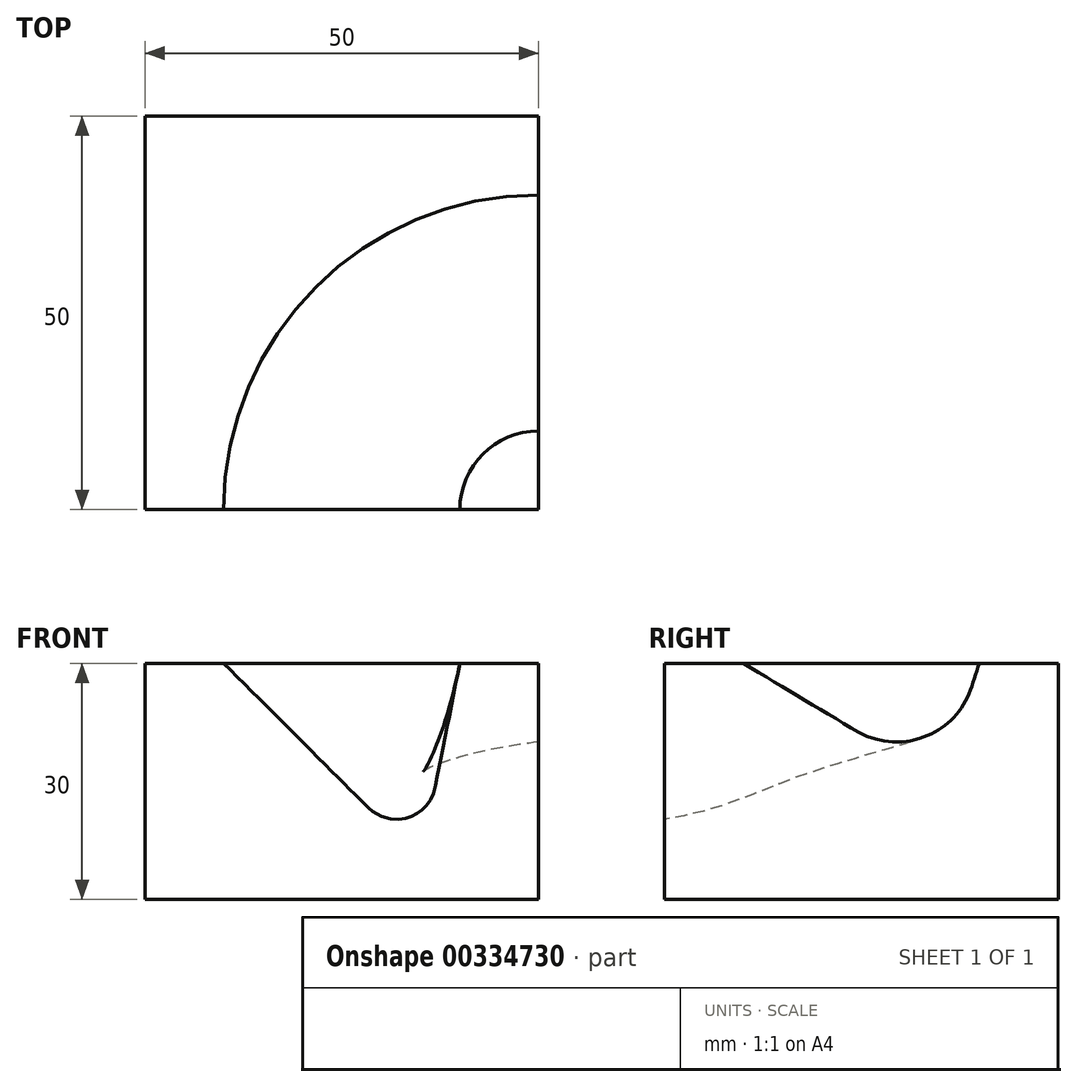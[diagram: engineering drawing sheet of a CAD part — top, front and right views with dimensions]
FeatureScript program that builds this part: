
annotation { "Feature Type Name" : "Feature", "Feature Type Description" : "" }
export const myFeature = defineFeature(function(context is Context, id is Id, definition is map)
    precondition{}
    {
        {
            var Q0;
            Q0=qCreatedBy(makeId("Top.planeOp"),FACE);
            var sketch = newSketch(context, id + "F0", { "sketchPlane" : qUnion([Q0])});
            skLineSegment(sketch, "E0.bottom", {"start": v(25, -25) * mm, "end": v(-25, -25) * mm});
            skLineSegment(sketch, "E0.top", {"start": v(25, 25) * mm, "end": v(-25, 25) * mm});
            skLineSegment(sketch, "E0.left", {"start": v(25, -25) * mm, "end": v(25, 25) * mm});
            skLineSegment(sketch, "E0.right", {"start": v(-25, -25) * mm, "end": v(-25, 25) * mm});
            skPoint(sketch, "E0.middle", {"position": v(0, 0) * mm});
            skSolve(sketch);
        }
        {
            var Q0;
            Q0 = qSketchRegion(id + "F0", true);
            extrude(context, id + "F1", {"entities" : qUnion([Q0]), "depth" : 30 * mm});
        }
        {
            var Q0;
            Q0=makeQuery(id+"F1.opExtrude","SWEPT_FACE",FACE,{"disambiguationData":[OSD([sQuery(id+"F0.wireOp",EDGE,"E0.bottom")])]});
            var sketch = newSketch(context, id + "F2", { "sketchPlane" : qUnion([Q0])});
            skLineSegment(sketch, "E1", {"start": v(-15, 30) * mm, "end": v(3.4, 11.6) * mm});
            skLineSegment(sketch, "E2", {"start": v(11.83, 14.16) * mm, "end": v(15, 30) * mm});
            skPoint(sketch, "E3.visualSharp", {"position": v(10, 5) * mm});
            skArc(sketch, "E3.filletArc", {"start": v(3.4, 11.6) * mm, "mid": v(8.38, 10.36) * mm, "end": v(11.83, 14.16) * mm});
            skSolve(sketch);
        }
        {
            var Q0;
            Q0=makeQuery(id+"F1.opExtrude","SWEPT_FACE",FACE,{"disambiguationData":[OSD([sQuery(id+"F0.wireOp",EDGE,"E0.left")])]});
            var sketch = newSketch(context, id + "F3", { "sketchPlane" : qUnion([Q0])});
            skLineSegment(sketch, "E4", {"start": v(-15, 30) * mm, "end": v(-0.69, 21.41) * mm});
            skLineSegment(sketch, "E5", {"start": v(13.94, 26.83) * mm, "end": v(15, 30) * mm});
            skPoint(sketch, "E6.visualSharp", {"position": v(10, 15) * mm});
            skArc(sketch, "E6.filletArc", {"start": v(-0.69, 21.41) * mm, "mid": v(7.92, 20.6) * mm, "end": v(13.94, 26.83) * mm});
            skSolve(sketch);
        }
        {
            var Q0;
            Q0=makeQuery(id+"F1.opExtrude","CAP_FACE",FACE,{"disambiguationData":[OSD([sQuery(id+"F0.wireOp",EDGE,"E0.bottom"),sQuery(id+"F0.wireOp",EDGE,"E0.top"),sQuery(id+"F0.wireOp",EDGE,"E0.left"),sQuery(id+"F0.wireOp",EDGE,"E0.right")])],"isStart":false});
            var sketch = newSketch(context, id + "F4", { "sketchPlane" : qUnion([Q0])});
            skCircle(sketch, "E7", {"center": v(25, -25) * mm, "radius": 10 * mm});
            skCircle(sketch, "E8", {"center": v(25, -25) * mm, "radius": 40 * mm});
            skSolve(sketch);
        }
        {
            var Q1;
            {var subQ0=sQuery(id+"F2.wireOp",EDGE,"E1");Q1=makeQuery(id+"F2.imprint","IMPRINT",FACE,{"disambiguationData":[TD([[makeQuery(id+"F2.imprint","IMPRINT",EDGE,{"derivedFrom":subQ0}),1.0]])]});}
            var Q2;
            {var subQ0=sQuery(id+"F3.wireOp",EDGE,"E4");Q2=makeQuery(id+"F3.imprint","IMPRINT",FACE,{"disambiguationData":[TD([[makeQuery(id+"F3.imprint","IMPRINT",EDGE,{"derivedFrom":subQ0}),1.0]])]});}
            var Q3;
            Q3=sQuery(id+"F4.wireOp",EDGE,"E8");
            var Q4;
            Q4=sQuery(id+"F4.wireOp",EDGE,"E7");
            loft(context, id + "F5", {"operationType" : NewBodyOperationType.REMOVE, "addGuides" : true, "sheetProfilesArray" : [{ "sheetProfileEntities" : qUnion([Q1]) }, { "sheetProfileEntities" : qUnion([Q2]) }], "guidesArray" : [{ "guideEntities" : qUnion([Q3]), "guideDerivativeType" : LoftGuideDerivativeType.DEFAULT, "guideDerivativeMagnitude" : 1 }, { "guideEntities" : qUnion([Q4]), "guideDerivativeType" : LoftGuideDerivativeType.DEFAULT, "guideDerivativeMagnitude" : 1 }]});
        }
    });
